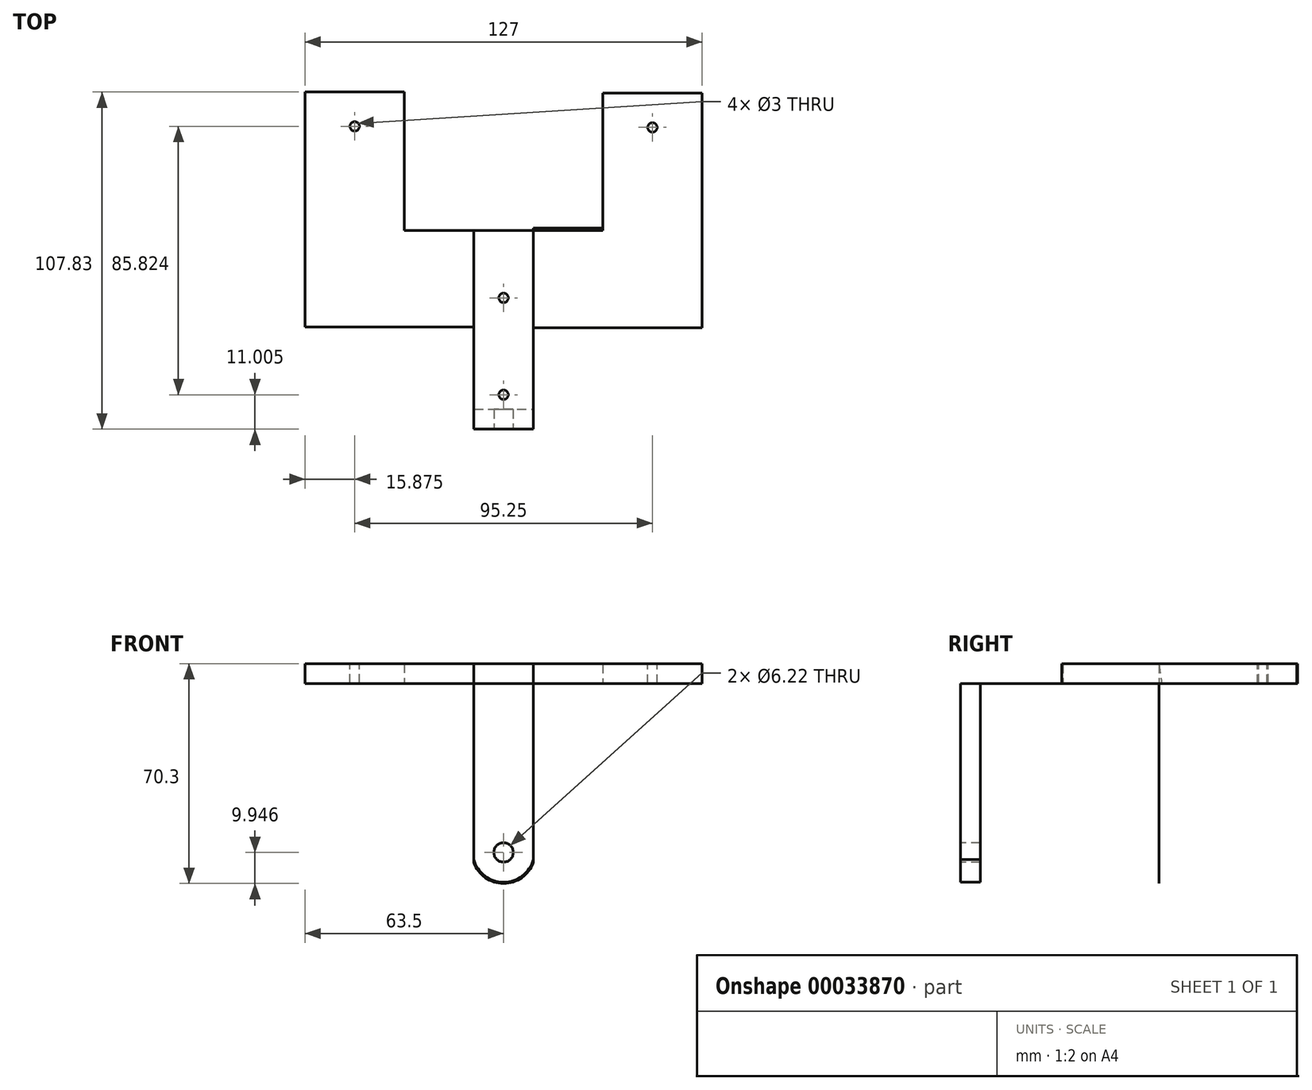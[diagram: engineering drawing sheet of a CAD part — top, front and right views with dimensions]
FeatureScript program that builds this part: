
annotation { "Feature Type Name" : "Feature", "Feature Type Description" : "" }
export const myFeature = defineFeature(function(context is Context, id is Id, definition is map)
    precondition{}
    {
        {
            var Q0;
            Q0=qCreatedBy(makeId("Front.planeOp"),FACE);
            var sketch = newSketch(context, id + "F0", { "sketchPlane" : qUnion([Q0])});
            skLineSegment(sketch, "E0", {"start": v(-9.53, 25.2) * mm, "end": v(9.53, 25.2) * mm});
            skLineSegment(sketch, "E1", {"start": v(9.53, 25.2) * mm, "end": v(9.53, -31.01) * mm});
            skLineSegment(sketch, "E2", {"start": v(-9.53, 25.2) * mm, "end": v(-9.53, -31.01) * mm});
            skArc(sketch, "E3", {"start": v(-9.53, -31.01) * mm, "mid": v(0, -38.3) * mm, "end": v(9.53, -31.01) * mm});
            skSolve(sketch);
        }
        {
            var Q0;
            Q0 = qSketchRegion(id + "F0", true);
            extrude(context, id + "F1", {"entities" : qUnion([Q0]), "depth" : 3.17 * mm});
        }
        {
            var Q0;
            Q0 = qSketchRegion(id + "F0", true);
            extrude(context, id + "F2", {"entities" : qUnion([Q0]), "operationType" : NewBodyOperationType.ADD, "oppositeDirection" : true, "depth" : 3.17 * mm});
        }
        {
            var Q0;
            Q0=qCreatedBy(makeId("Front.planeOp"),FACE);
            var sketch = newSketch(context, id + "F3", { "sketchPlane" : qUnion([Q0])});
            skCircle(sketch, "E4", {"center": v(0, -28.73) * mm, "radius": 3.11 * mm});
            skLineSegment(sketch, "E5", {"start": v(0, -28.73) * mm, "end": v(0, -38.26) * mm});
            skSolve(sketch);
        }
        {
            var Q0;
            Q0 = qSketchRegion(id + "F3", true);
            extrude(context, id + "F4", {"entities" : qUnion([Q0]), "operationType" : NewBodyOperationType.REMOVE, "oppositeDirection" : true, "depth" : 25.4 * mm});
        }
        {
            var Q0;
            Q0 = qSketchRegion(id + "F3", true);
            extrude(context, id + "F5", {"entities" : qUnion([Q0]), "operationType" : NewBodyOperationType.REMOVE, "depth" : 25.4 * mm});
        }
        {
            var Q0;
            {var subQ0=sQuery(id+"F0.wireOp",EDGE,"E0");Q0=makeQuery(id+"F2.boolean.opBoolean","MERGE",FACE,{"derivedFrom":[makeQuery(id+"F1.opExtrude","SWEPT_FACE",FACE,{"disambiguationData":[OSD([subQ0])]}),makeQuery(id+"F2.opExtrude","SWEPT_FACE",FACE,{"disambiguationData":[OSD([subQ0])]})]});}
            var sketch = newSketch(context, id + "F6", { "sketchPlane" : qUnion([Q0])});
            skLineSegment(sketch, "E6", {"start": v(-9.53, -3.18) * mm, "end": v(-9.53, 60.33) * mm});
            skPoint(sketch, "E7.endSnap0", {"position": v(9.53, 0) * mm});
            skLineSegment(sketch, "E8", {"start": v(9.53, -3.18) * mm, "end": v(9.53, 60.33) * mm});
            skLineSegment(sketch, "E9", {"start": v(9.53, 60.33) * mm, "end": v(-9.53, 60.33) * mm});
            skLineSegment(sketch, "E10", {"start": v(-9.53, -3.18) * mm, "end": v(9.53, -3.18) * mm});
            skSolve(sketch);
        }
        {
            var Q0;
            Q0 = qSketchRegion(id + "F6", true);
            extrude(context, id + "F7", {"entities" : qUnion([Q0]), "operationType" : NewBodyOperationType.ADD, "depth" : 1 / 101.6 * mm});
        }
        {
            var Q0;
            Q0=makeQuery(id+"F7.opExtrude","SWEPT_FACE",FACE,{"disambiguationData":[OSD([sQuery(id+"F6.wireOp",EDGE,"E9")])]});
            var sketch = newSketch(context, id + "F8", { "sketchPlane" : qUnion([Q0])});
            skPoint(sketch, "E11.endSnap0", {"position": v(-9.53, 28.38) * mm});
            skArc(sketch, "E12", {"start": v(-9.53, -31.94) * mm, "mid": v(0, -38.68) * mm, "end": v(9.53, -31.94) * mm});
            skLineSegment(sketch, "E13", {"start": v(-9.53, 31.56) * mm, "end": v(-9.53, -31.94) * mm});
            skLineSegment(sketch, "E14", {"start": v(9.53, 31.56) * mm, "end": v(9.53, -31.94) * mm});
            skLineSegment(sketch, "E15", {"start": v(-9.53, 31.56) * mm, "end": v(9.53, 31.56) * mm});
            skSolve(sketch);
        }
        {
            var Q0;
            Q0 = qSketchRegion(id + "F8", true);
            extrude(context, id + "F9", {"entities" : qUnion([Q0]), "oppositeDirection" : true, "depth" : 1 / 101.6 * mm});
        }
        {
            var Q0;
            Q0 = qSketchRegion(id + "F3", true);
            extrude(context, id + "F10", {"entities" : qUnion([Q0]), "operationType" : NewBodyOperationType.REMOVE, "oppositeDirection" : true, "depth" : 2540 * mm});
        }
        {
            var Q0;
            Q0=makeQuery(id+"F7.opExtrude","CAP_FACE",FACE,{"disambiguationData":[OSD([sQuery(id+"F6.wireOp",EDGE,"E6"),sQuery(id+"F6.wireOp",EDGE,"E8"),sQuery(id+"F6.wireOp",EDGE,"E9"),sQuery(id+"F6.wireOp",EDGE,"E10")])],"isStart":false});
            var sketch = newSketch(context, id + "F11", { "sketchPlane" : qUnion([Q0])});
            skCircle(sketch, "E16", {"center": v(0, 7.82) * mm, "radius": 1.5 * mm});
            skCircle(sketch, "E17", {"center": v(0, 38.8) * mm, "radius": 1.5 * mm});
            skSolve(sketch);
        }
        {
            var Q0;
            Q0 = qSketchRegion(id + "F11", true);
            extrude(context, id + "F12", {"entities" : qUnion([Q0]), "operationType" : NewBodyOperationType.REMOVE, "oppositeDirection" : true, "depth" : 25.4 * mm});
        }
        {
            var Q0;
            {var subQ0=sQuery(id+"F0.wireOp",EDGE,"E1");Q0=makeQuery(id+"F7.boolean.opBoolean","MERGE",FACE,{"derivedFrom":[makeQuery(id+"F2.boolean.opBoolean","MERGE",FACE,{"derivedFrom":[makeQuery(id+"F1.opExtrude","SWEPT_FACE",FACE,{"disambiguationData":[OSD([subQ0])]}),makeQuery(id+"F2.opExtrude","SWEPT_FACE",FACE,{"disambiguationData":[OSD([subQ0])]})]}),makeQuery(id+"F7.opExtrude","SWEPT_FACE",FACE,{"disambiguationData":[OSD([sQuery(id+"F6.wireOp",EDGE,"E8")])]})]});}
            var sketch = newSketch(context, id + "F13", { "sketchPlane" : qUnion([Q0])});
            skLineSegment(sketch, "E18", {"start": v(104.33, 31.56) * mm, "end": v(104.33, 25.2) * mm});
            skLineSegment(sketch, "E19", {"start": v(29.18, 31.56) * mm, "end": v(104.33, 31.56) * mm});
            skLineSegment(sketch, "E20", {"start": v(104.33, 25.2) * mm, "end": v(29.18, 25.2) * mm});
            skLineSegment(sketch, "E21", {"start": v(29.18, 25.2) * mm, "end": v(29.18, 31.56) * mm});
            skSolve(sketch);
        }
        {
            var Q0;
            Q0 = qSketchRegion(id + "F13", true);
            extrude(context, id + "F14", {"entities" : qUnion([Q0]), "operationType" : NewBodyOperationType.ADD, "depth" : 53.97 * mm});
        }
        {
            var Q0;
            Q0=makeQuery(id+"F14.boolean.opBoolean","MERGE",FACE,{"derivedFrom":[makeQuery(id+"F9.opExtrude","SWEPT_FACE",FACE,{"disambiguationData":[OSD([sQuery(id+"F8.wireOp",EDGE,"E15")])]}),makeQuery(id+"F7.opExtrude","CAP_FACE",FACE,{"disambiguationData":[OSD([sQuery(id+"F6.wireOp",EDGE,"E6"),sQuery(id+"F6.wireOp",EDGE,"E8"),sQuery(id+"F6.wireOp",EDGE,"E9"),sQuery(id+"F6.wireOp",EDGE,"E10")])],"isStart":false}),makeQuery(id+"F14.opExtrude","SWEPT_FACE",FACE,{"disambiguationData":[OSD([sQuery(id+"F13.wireOp",EDGE,"7d0c347f-23ee-4703-af74-5e1430c4c102")])]})]});
            var sketch = newSketch(context, id + "F15", { "sketchPlane" : qUnion([Q0])});
            skCircle(sketch, "E22", {"center": v(47.62, 93.33) * mm, "radius": 1.5 * mm});
            skSolve(sketch);
        }
        {
            var Q0;
            Q0 = qSketchRegion(id + "F15", true);
            extrude(context, id + "F16", {"entities" : qUnion([Q0]), "operationType" : NewBodyOperationType.REMOVE, "oppositeDirection" : true, "depth" : 25 * mm});
        }
        {
            var Q0;
            {var subQ0=sQuery(id+"F0.wireOp",EDGE,"E2");Q0=makeQuery(id+"F14.boolean.opBoolean","MERGE",FACE,{"derivedFrom":[makeQuery(id+"F7.boolean.opBoolean","MERGE",FACE,{"derivedFrom":[makeQuery(id+"F2.boolean.opBoolean","MERGE",FACE,{"derivedFrom":[makeQuery(id+"F1.opExtrude","SWEPT_FACE",FACE,{"disambiguationData":[OSD([subQ0])]}),makeQuery(id+"F2.opExtrude","SWEPT_FACE",FACE,{"disambiguationData":[OSD([subQ0])]})]}),makeQuery(id+"F7.opExtrude","SWEPT_FACE",FACE,{"disambiguationData":[OSD([sQuery(id+"F6.wireOp",EDGE,"E6")])]})]}),makeQuery(id+"F9.opExtrude","SWEPT_FACE",FACE,{"disambiguationData":[OSD([sQuery(id+"F8.wireOp",EDGE,"E14")])]})]});}
            var sketch = newSketch(context, id + "F17", { "sketchPlane" : qUnion([Q0])});
            skLineSegment(sketch, "E23", {"start": v(-104.65, 25.27) * mm, "end": v(-104.65, 31.62) * mm});
            skLineSegment(sketch, "E24", {"start": v(-104.65, 31.62) * mm, "end": v(-29.5, 31.62) * mm});
            skLineSegment(sketch, "E25", {"start": v(-29.5, 31.62) * mm, "end": v(-29.5, 25.27) * mm});
            skLineSegment(sketch, "E26", {"start": v(-29.5, 25.27) * mm, "end": v(-104.65, 25.27) * mm});
            skSolve(sketch);
        }
        {
            var Q0;
            Q0 = qSketchRegion(id + "F17", true);
            var Q1;
            Q1=sQuery(id+"F17.wireOp",EDGE,"E23");
            var Q2;
            Q2=sQuery(id+"F17.wireOp",EDGE,"E24");
            var Q3;
            Q3=sQuery(id+"F17.wireOp",EDGE,"E25");
            var Q4;
            Q4=sQuery(id+"F17.wireOp",EDGE,"E26");
            extrude(context, id + "F18", {"entities" : qUnion([Q0]), "operationType" : NewBodyOperationType.ADD, "surfaceEntities" : qUnion([Q1, Q2, Q3, Q4]), "depth" : 53.97 * mm});
        }
        {
            var Q0;
            Q0=makeQuery(id+"F18.opExtrude","SWEPT_FACE",FACE,{"disambiguationData":[OSD([sQuery(id+"F17.wireOp",EDGE,"E24")])]});
            var sketch = newSketch(context, id + "F19", { "sketchPlane" : qUnion([Q0])});
            skCircle(sketch, "E27", {"center": v(-47.63, 93.65) * mm, "radius": 1.5 * mm});
            skSolve(sketch);
        }
        {
            var Q0;
            Q0 = qSketchRegion(id + "F19", true);
            extrude(context, id + "F20", {"entities" : qUnion([Q0]), "operationType" : NewBodyOperationType.REMOVE, "oppositeDirection" : true, "depth" : 25 * mm});
        }
        {
            var Q0;
            Q0=makeQuery(id+"F14.opExtrude","CAP_FACE",FACE,{"disambiguationData":[OSD([sQuery(id+"F13.wireOp",EDGE,"E18"),sQuery(id+"F13.wireOp",EDGE,"E19"),sQuery(id+"F13.wireOp",EDGE,"E20"),sQuery(id+"F13.wireOp",EDGE,"E21")])],"isStart":true});
            var sketch = newSketch(context, id + "F21", { "sketchPlane" : qUnion([Q0])});
            skLineSegment(sketch, "E28", {"start": v(-104.33, 25.2) * mm, "end": v(-104.33, 31.56) * mm});
            skLineSegment(sketch, "E29", {"start": v(-104.33, 31.56) * mm, "end": v(-60.33, 31.56) * mm});
            skLineSegment(sketch, "E30", {"start": v(-60.33, 31.56) * mm, "end": v(-61.12, 25.2) * mm});
            skLineSegment(sketch, "E31", {"start": v(-61.12, 25.2) * mm, "end": v(-104.33, 25.2) * mm});
            skSolve(sketch);
        }
        {
            var Q0;
            Q0 = qSketchRegion(id + "F21", true);
            extrude(context, id + "F22", {"entities" : qUnion([Q0]), "operationType" : NewBodyOperationType.REMOVE, "oppositeDirection" : true, "depth" : 22.22 * mm});
        }
        {
            var Q0;
            Q0=makeQuery(id+"F18.opExtrude","CAP_FACE",FACE,{"disambiguationData":[OSD([sQuery(id+"F17.wireOp",EDGE,"E23"),sQuery(id+"F17.wireOp",EDGE,"E24"),sQuery(id+"F17.wireOp",EDGE,"E25"),sQuery(id+"F17.wireOp",EDGE,"E26")])],"isStart":true});
            var sketch = newSketch(context, id + "F23", { "sketchPlane" : qUnion([Q0])});
            skLineSegment(sketch, "E32.bottom", {"start": v(104.65, 31.62) * mm, "end": v(60.33, 31.62) * mm});
            skLineSegment(sketch, "E32.top", {"start": v(104.65, 25.27) * mm, "end": v(60.33, 25.27) * mm});
            skLineSegment(sketch, "E32.left", {"start": v(104.65, 31.62) * mm, "end": v(104.65, 25.27) * mm});
            skLineSegment(sketch, "E32.right", {"start": v(60.33, 31.62) * mm, "end": v(60.33, 25.27) * mm});
            skSolve(sketch);
        }
        {
            var Q0;
            Q0 = qSketchRegion(id + "F23", true);
            extrude(context, id + "F24", {"entities" : qUnion([Q0]), "operationType" : NewBodyOperationType.REMOVE, "oppositeDirection" : true, "depth" : 22.22 * mm});
        }
    });
